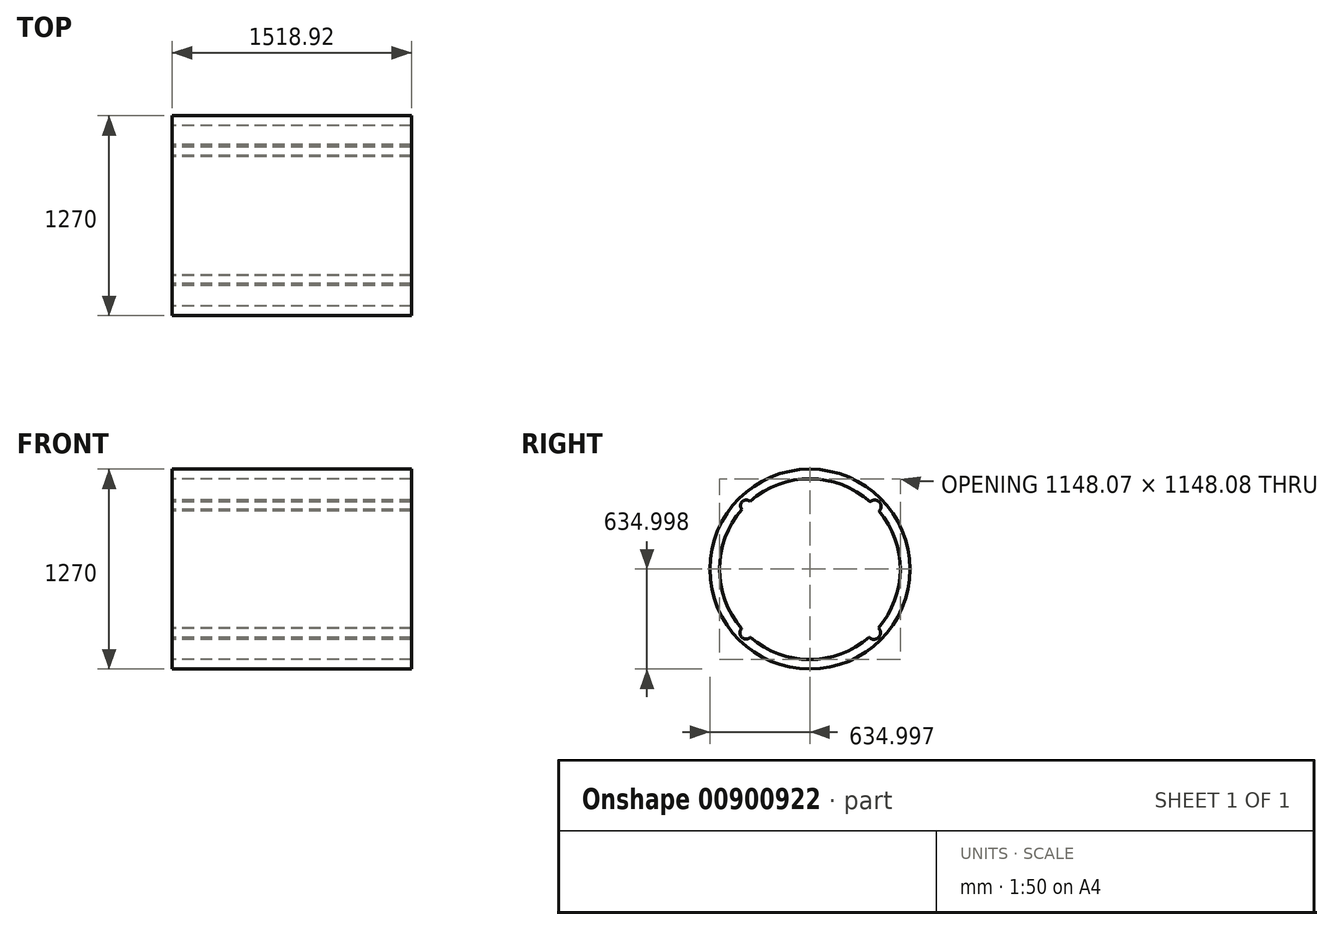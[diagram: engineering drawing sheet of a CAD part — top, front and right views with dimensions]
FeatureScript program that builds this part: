
annotation { "Feature Type Name" : "Feature", "Feature Type Description" : "" }
export const myFeature = defineFeature(function(context is Context, id is Id, definition is map)
    precondition{}
    {
        {
            var Q0;
            Q0=qCreatedBy(makeId("Right.planeOp"),FACE);
            var sketch = newSketch(context, id + "F0", { "sketchPlane" : qUnion([Q0])});
            skCircle(sketch, "E0", {"center": v(0, 0) * mm, "radius": 635 * mm});
            skCircle(sketch, "E1", {"center": v(0, 0) * mm, "radius": 574.04 * mm});
            skLineSegment(sketch, "E2", {"start": v(0, 0) * mm, "end": v(328.03, 568.17) * mm});
            skLineSegment(sketch, "E3", {"start": v(0, 0) * mm, "end": v(0, 877.7) * mm});
            skLineSegment(sketch, "E4", {"start": v(0, 0) * mm, "end": v(-364.4, -631.17) * mm});
            skLineSegment(sketch, "E5", {"start": v(0, 0) * mm, "end": v(-483.76, 483.76) * mm});
            skLineSegment(sketch, "E6", {"start": v(0, 0) * mm, "end": v(-484.48, -484.48) * mm});
            skLineSegment(sketch, "E7", {"start": v(0, 0) * mm, "end": v(487.47, -487.47) * mm});
            skLineSegment(sketch, "E8", {"start": v(0, 0) * mm, "end": v(470.65, 470.65) * mm});
            skLineSegment(sketch, "E9", {"start": v(-126.68, 622.24) * mm, "end": v(-126.68, 559.89) * mm});
            skLineSegment(sketch, "E10", {"start": v(127.32, 559.74) * mm, "end": v(127.32, 622.1) * mm});
            skLineSegment(sketch, "E11", {"start": v(435.94, -373.47) * mm, "end": v(480.98, -414.59) * mm});
            skLineSegment(sketch, "E12", {"start": v(376.82, -433.04) * mm, "end": v(419.54, -476.66) * mm});
            skLineSegment(sketch, "E13", {"start": v(-432.63, -377.3) * mm, "end": v(-475.83, -420.5) * mm});
            skLineSegment(sketch, "E14", {"start": v(-418.53, -477.55) * mm, "end": v(-377.9, -432.1) * mm});
            skLineSegment(sketch, "E15", {"start": v(-430.9, 379.27) * mm, "end": v(-471.8, 425) * mm});
            skLineSegment(sketch, "E16", {"start": v(-423.49, 473.16) * mm, "end": v(-380.3, 429.99) * mm});
            skLineSegment(sketch, "E17", {"start": v(439.94, 368.75) * mm, "end": v(483.2, 412) * mm});
            skLineSegment(sketch, "E18", {"start": v(483.2, 412) * mm, "end": v(426.6, 470.35) * mm});
            skLineSegment(sketch, "E19", {"start": v(426.6, 470.35) * mm, "end": v(383.45, 427.19) * mm});
            skLineSegment(sketch, "E20", {"start": v(383.45, 427.19) * mm, "end": v(439.94, 368.75) * mm});
            skArc(sketch, "E21", {"start": v(-380.3, 429.99) * mm, "mid": v(-429.56, 428.52) * mm, "end": v(-430.9, 379.27) * mm});
            skArc(sketch, "E22", {"start": v(439.94, 368.75) * mm, "mid": v(441.41, 426.7) * mm, "end": v(383.45, 427.19) * mm});
            skArc(sketch, "E23", {"start": v(-432.63, -377.3) * mm, "mid": v(-432.65, -432.05) * mm, "end": v(-377.9, -432.1) * mm});
            skArc(sketch, "E24", {"start": v(376.82, -433.04) * mm, "mid": v(436.6, -433.24) * mm, "end": v(435.94, -373.47) * mm});
            skSolve(sketch);
        }
        {
            var Q0;
            Q0 = qSketchRegion(id + "F0", true);
            extrude(context, id + "F1", {"entities" : qUnion([Q0]), "depth" : 1518.92 * mm, "offsetDistance" : 25.4 * mm});
        }
    });
